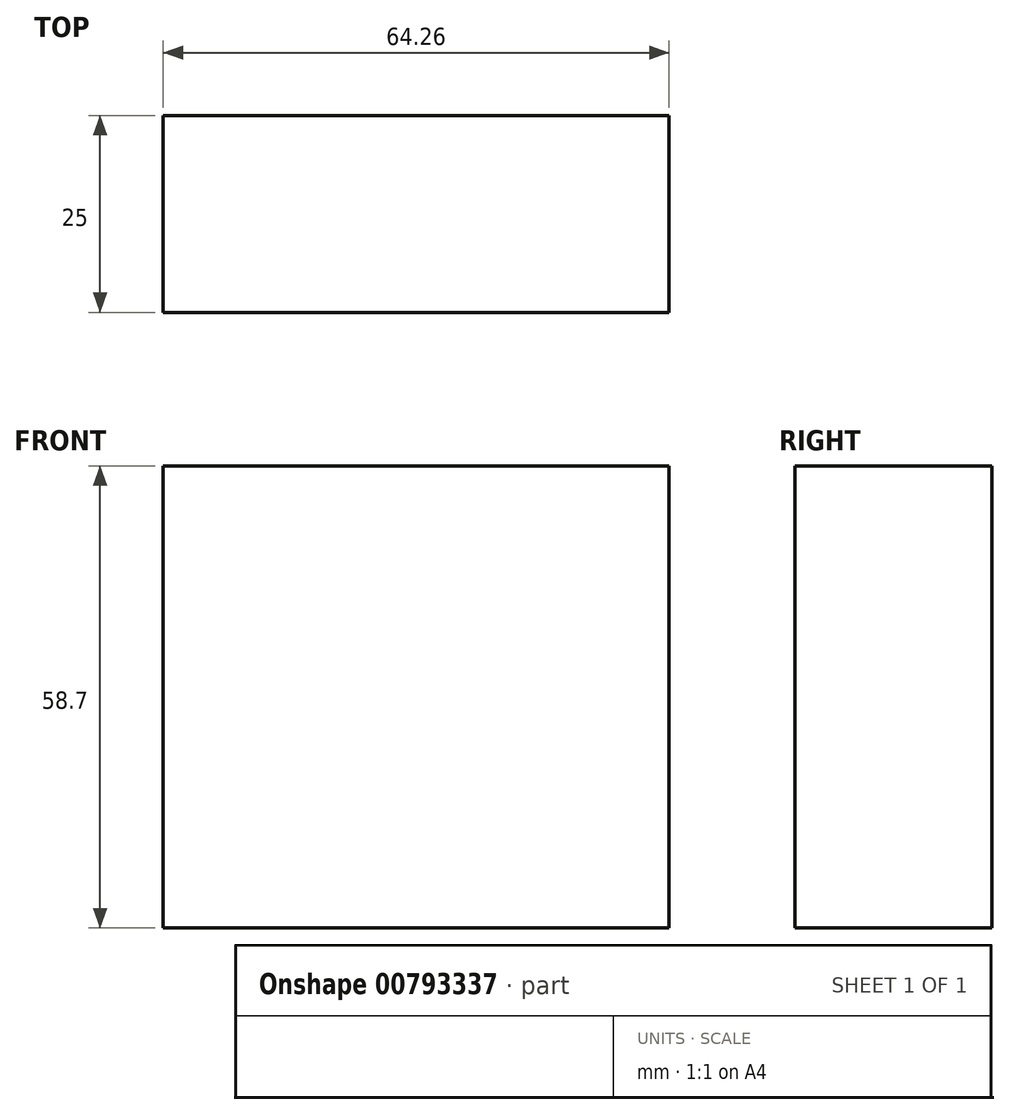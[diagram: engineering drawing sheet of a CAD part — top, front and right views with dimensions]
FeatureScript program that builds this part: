
annotation { "Feature Type Name" : "Feature", "Feature Type Description" : "" }
export const myFeature = defineFeature(function(context is Context, id is Id, definition is map)
    precondition{}
    {
        {
            var Q0;
            Q0=qCreatedBy(makeId("Front.planeOp"),FACE);
            var sketch = newSketch(context, id + "F0", { "sketchPlane" : qUnion([Q0])});
            skLineSegment(sketch, "E0.bottom", {"start": v(-129.66, 25.05) * mm, "end": v(-65.4, 25.05) * mm});
            skLineSegment(sketch, "E0.top", {"start": v(-129.66, -33.65) * mm, "end": v(-65.4, -33.65) * mm});
            skLineSegment(sketch, "E0.left", {"start": v(-129.66, 25.05) * mm, "end": v(-129.66, -33.65) * mm});
            skLineSegment(sketch, "E0.right", {"start": v(-65.4, 25.05) * mm, "end": v(-65.4, -33.65) * mm});
            skSolve(sketch);
        }
        {
            var Q0;
            Q0 = qSketchRegion(id + "F0", true);
            extrude(context, id + "F1", {"entities" : qUnion([Q0]), "depth" : 25 * mm, "offsetDistance" : 25 * mm});
        }
    });
